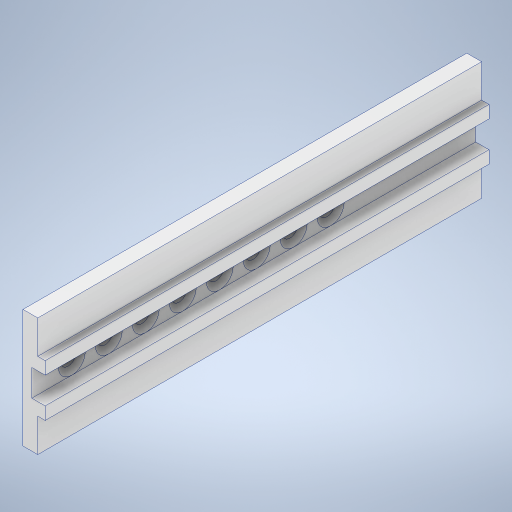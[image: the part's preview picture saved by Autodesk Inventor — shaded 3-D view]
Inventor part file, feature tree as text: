
AUTODESK INVENTOR PART (.ipt)
format: ipt  version: 2024 (Build 280153000, 153)  size: 331,264 bytes
history: native  units: mm
features: extrude x3, sketch x3, chamfer x1
ambient origin geometry x8: Origin, YZ Plane, XZ Plane, XY Plane, X Axis, Y Axis, Z Axis, Center Point
bodies: Solid1 (feature_tree)
feature tree (7):
  extrude  "Extrusion1"  Depth=160.0mm TaperAngle=0.0deg
  extrude  "Extrusion2"  Depth=25.0mm
  extrude  "Extrusion3"  Depth=45.0mm
  chamfer  "Chamfer1"  Distance=45.0mm
  sketch  "Sketch1"  dims[d0=600.0mm d1=160.0mm d2=0.0mm]
  sketch  "Sketch2"  dims[d4=25.0mm d5=25.0mm]
  sketch  "Sketch3"  dims[d6=10.0mm d7=45.0mm d8=45.0mm d9=18.0mm d10=36.0mm d11=80.0mm d12=80.0mm d13=150.0mm d14=0.0mm d15=30.0mm d16=90.0mm d18=50.0mm d19=10.0mm d21=10.0mm d23=25.0mm d24=0.0mm d25=8.0mm d26=5.0mm d27=45.0deg d28=39.130435mm]
